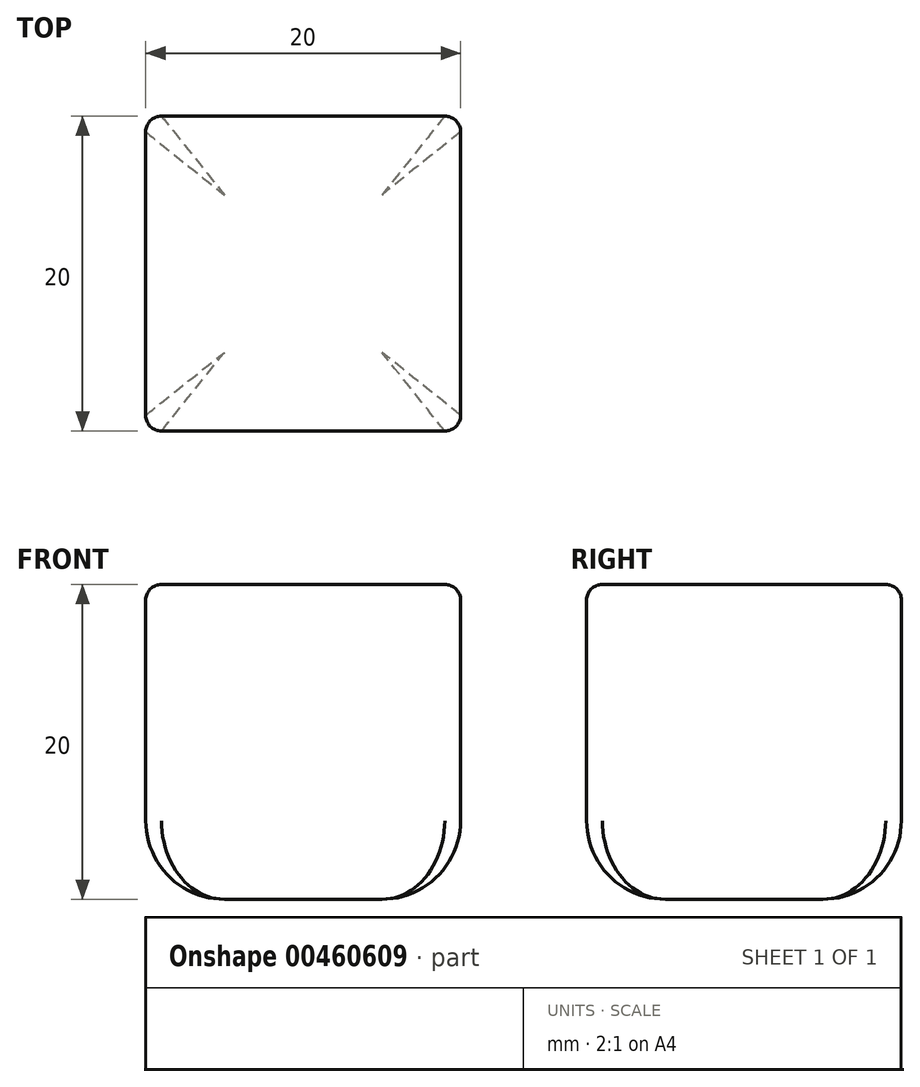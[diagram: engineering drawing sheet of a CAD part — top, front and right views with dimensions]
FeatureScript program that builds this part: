
annotation { "Feature Type Name" : "Feature", "Feature Type Description" : "" }
export const myFeature = defineFeature(function(context is Context, id is Id, definition is map)
    precondition{}
    {
        {
            var Q0;
            Q0=qCreatedBy(makeId("Front.planeOp"),FACE);
            var sketch = newSketch(context, id + "F0", { "sketchPlane" : qUnion([Q0])});
            skLineSegment(sketch, "E0.bottom", {"start": v(-15, 60) * mm, "end": v(5, 60) * mm});
            skLineSegment(sketch, "E0.top", {"start": v(-15, 40) * mm, "end": v(5, 40) * mm});
            skLineSegment(sketch, "E0.left", {"start": v(-15, 60) * mm, "end": v(-15, 40) * mm});
            skLineSegment(sketch, "E0.right", {"start": v(5, 60) * mm, "end": v(5, 40) * mm});
            skSolve(sketch);
        }
        {
            var Q0;
            Q0=makeQuery(id+"F0.imprint","IMPRINT",FACE,{"disambiguationData":[TD([[makeQuery(id+"F0.imprint","IMPRINT",EDGE,{"derivedFrom":sQuery(id+"F0.wireOp",EDGE,"E0.bottom")}),-1.0]])]});
            extrude(context, id + "F1", {"entities" : qUnion([Q0]), "depth" : 20 * mm});
        }
        {
            var Q0;
            Q0=makeQuery(id+"F1.opExtrude","SWEPT_FACE",FACE,{"disambiguationData":[OSD([sQuery(id+"F0.wireOp",EDGE,"E0.top")])]});
            fillet(context, id + "F2", {"entities" : qUnion([Q0]), "radius" : 5 * mm, "tangentPropagation" : true, "allowEdgeOverflow" : false});
        }
        {
            var Q0;
            Q0=makeQuery(id+"F1.opExtrude","SWEPT_FACE",FACE,{"disambiguationData":[OSD([sQuery(id+"F0.wireOp",EDGE,"E0.bottom")])]});
            fillet(context, id + "F3", {"entities" : qUnion([Q0]), "radius" : 1 * mm, "tangentPropagation" : true, "allowEdgeOverflow" : false});
        }
        {
            var Q0;
            Q0=makeQuery(id+"F1.opExtrude","SWEPT_FACE",FACE,{"disambiguationData":[OSD([sQuery(id+"F0.wireOp",EDGE,"E0.right")])]});
            fillet(context, id + "F4", {"entities" : qUnion([Q0]), "radius" : 1 * mm, "tangentPropagation" : true, "allowEdgeOverflow" : false});
        }
        {
            var Q0;
            Q0=makeQuery(id+"F1.opExtrude","SWEPT_FACE",FACE,{"disambiguationData":[OSD([sQuery(id+"F0.wireOp",EDGE,"E0.left")])]});
            fillet(context, id + "F5", {"entities" : qUnion([Q0]), "radius" : 1 * mm, "tangentPropagation" : true, "allowEdgeOverflow" : false});
        }
    });
